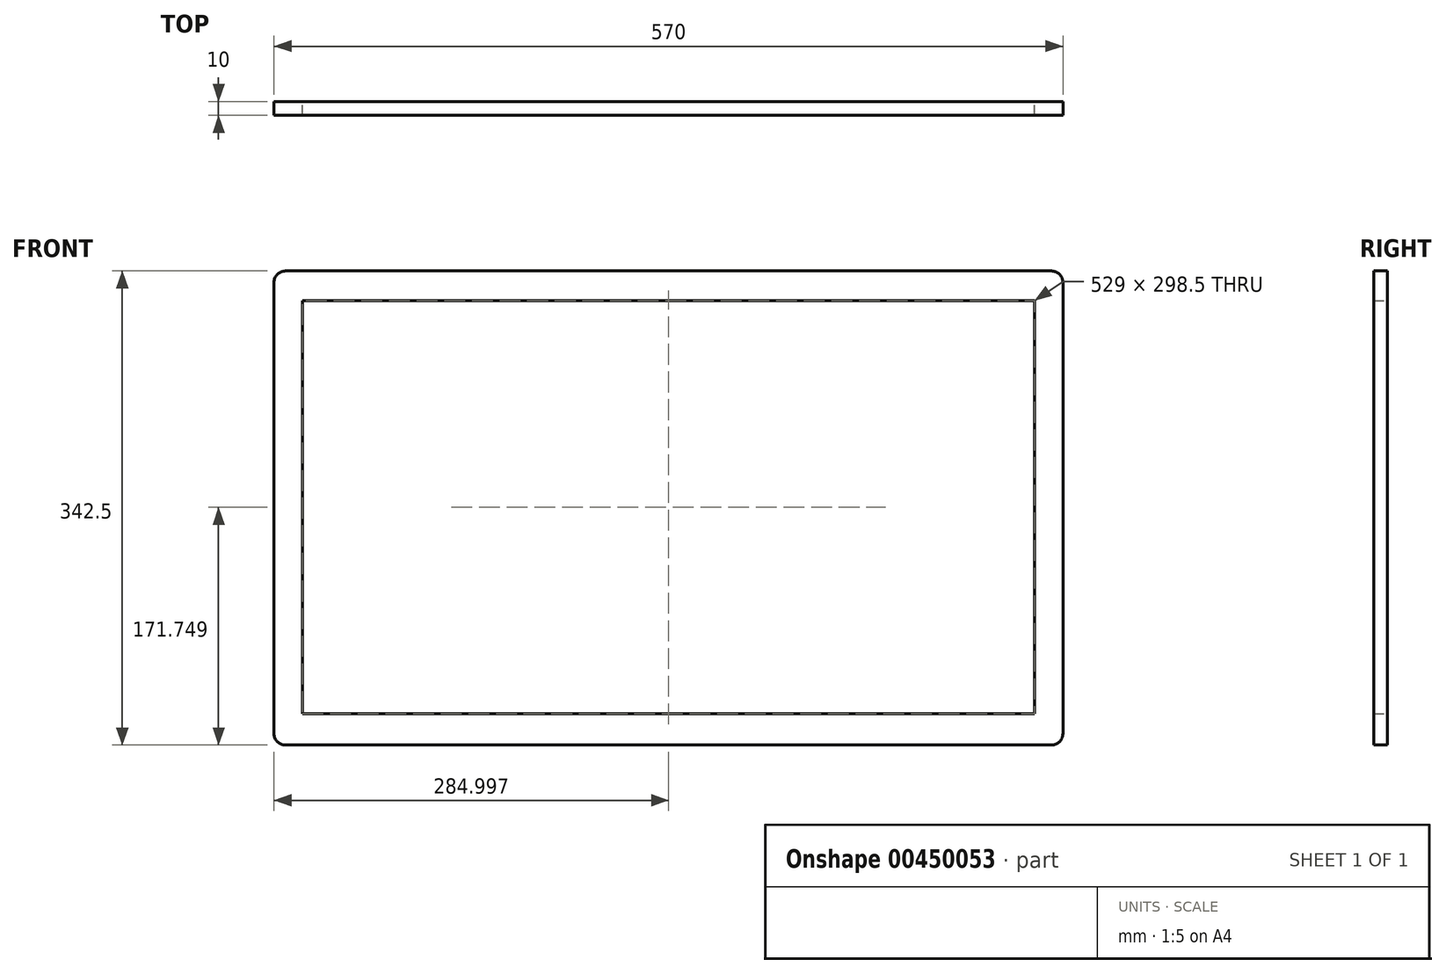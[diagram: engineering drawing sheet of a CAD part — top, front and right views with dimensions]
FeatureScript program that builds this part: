
annotation { "Feature Type Name" : "Feature", "Feature Type Description" : "" }
export const myFeature = defineFeature(function(context is Context, id is Id, definition is map)
    precondition{}
    {
        {
            var Q0;
            Q0=qCreatedBy(makeId("Front.planeOp"),FACE);
            var sketch = newSketch(context, id + "F0", { "sketchPlane" : qUnion([Q0])});
            skLineSegment(sketch, "E0.bottom", {"start": v(-254.65, 187.26) * mm, "end": v(298.95, 187.26) * mm});
            skLineSegment(sketch, "E0.top", {"start": v(-254.65, -155.24) * mm, "end": v(298.95, -155.24) * mm});
            skLineSegment(sketch, "E0.left", {"start": v(-262.85, 179.06) * mm, "end": v(-262.85, -147.04) * mm});
            skLineSegment(sketch, "E0.right", {"start": v(307.15, 179.06) * mm, "end": v(307.15, -147.04) * mm});
            skPoint(sketch, "E1.visualSharp", {"position": v(-262.85, 187.26) * mm});
            skArc(sketch, "E1.filletArc", {"start": v(-254.65, 187.26) * mm, "mid": v(-260.45, 184.86) * mm, "end": v(-262.85, 179.06) * mm});
            skPoint(sketch, "E2.visualSharp", {"position": v(307.15, 187.26) * mm});
            skArc(sketch, "E2.filletArc", {"start": v(307.15, 179.06) * mm, "mid": v(304.75, 184.86) * mm, "end": v(298.95, 187.26) * mm});
            skPoint(sketch, "E3.visualSharp", {"position": v(307.15, -155.24) * mm});
            skArc(sketch, "E3.filletArc", {"start": v(298.95, -155.24) * mm, "mid": v(304.75, -152.84) * mm, "end": v(307.15, -147.04) * mm});
            skPoint(sketch, "E4.visualSharp", {"position": v(-262.85, -155.24) * mm});
            skArc(sketch, "E4.filletArc", {"start": v(-262.85, -147.04) * mm, "mid": v(-260.45, -152.84) * mm, "end": v(-254.65, -155.24) * mm});
            skLineSegment(sketch, "E5.bottom", {"start": v(-242.35, 165.76) * mm, "end": v(286.65, 165.76) * mm});
            skLineSegment(sketch, "E5.top", {"start": v(-242.35, -132.74) * mm, "end": v(286.65, -132.74) * mm});
            skLineSegment(sketch, "E5.left", {"start": v(-242.35, 165.76) * mm, "end": v(-242.35, -132.74) * mm});
            skLineSegment(sketch, "E5.right", {"start": v(286.65, 165.76) * mm, "end": v(286.65, -132.74) * mm});
            skSolve(sketch);
        }
        {
            var Q0;
            Q0 = qSketchRegion(id + "F0", true);
            extrude(context, id + "F1", {"entities" : qUnion([Q0]), "depth" : 10 * mm});
        }
        {
            var Q0;
            Q0=makeQuery(id+"F0.imprint","IMPRINT",FACE,{"disambiguationData":[TD([[makeQuery(id+"F0.imprint","IMPRINT",EDGE,{"derivedFrom":sQuery(id+"F0.wireOp",EDGE,"E5.bottom")}),-1.0]])]});
            extrude(context, id + "F2", {"entities" : qUnion([Q0]), "depth" : 10 * mm});
        }
    });
